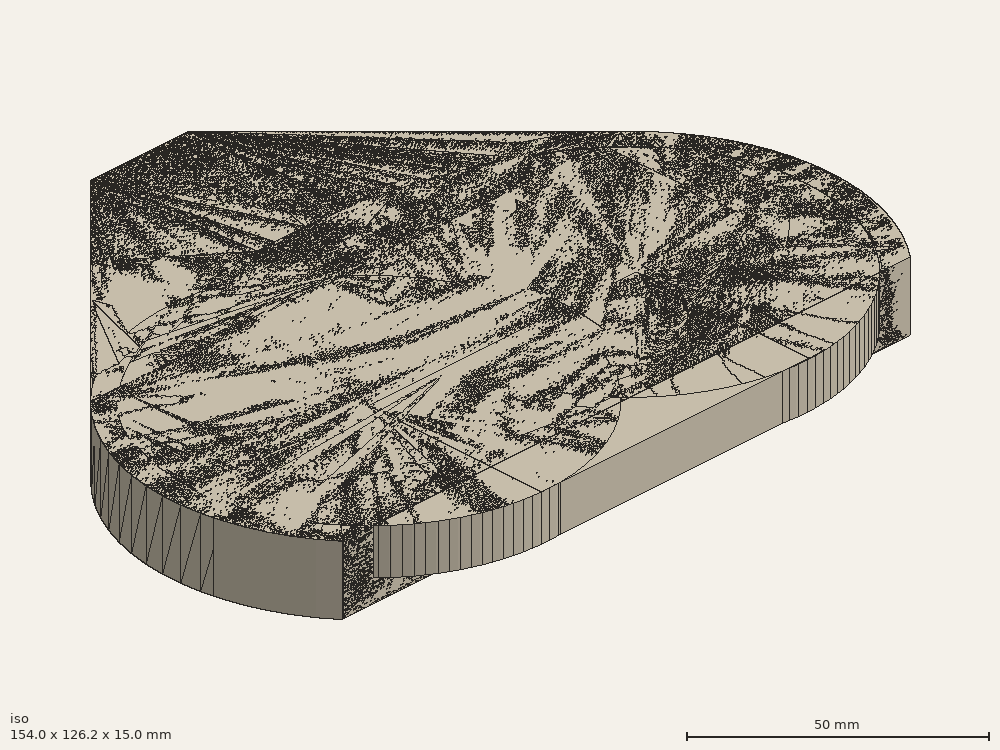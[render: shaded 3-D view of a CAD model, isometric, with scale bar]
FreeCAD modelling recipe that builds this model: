
FCSTD DOCUMENT  (FreeCAD 0.18.4R)
Label: Szajzuhany.Tarto
License: All rights reserved
LicenseURL: http://en.wikipedia.org/wiki/All_rights_reserved
objects: Part::Part2DObjectPython×82, Part::Extrusion×43, Part::Cut×29, Part::Feature×22, Part::MultiFuse×13, Part::FeaturePython×8, Part::Box×6, App::DocumentObjectGroup×4
note: 203 computed .brp shape members not serialized (recipe doc carries the construction recipe); baked Part::Feature solids carry a one-line shape summary decoded from their .brp

FEATURE [Part::Feature] Cut009001_solid  label="Cut010 (Solid)"
  shape: bbox 154 x 114.1 x 15 mm, 51 faces (baked)
FEATURE [Part::Part2DObjectPython] Wire  # Draft 2D object (typed FeaturePython)
  ChamferSize = 0
  Closed = true
  End = (-2.4044,46.1222,15)
  FilletRadius = 0
  Length = 57.6433
  MakeFace = true
  Placement = pos=(-7.75138,65.6617,15) rot=(1,0,0;3.14159rad)
  Points = (4) [(0,0,0),(-8.81629,8.81629,0),(-5.09821,22.4033,-1.11644e-11),(5.34698,19.5396,-1.11644e-11)]
  Start = (-7.75138,65.6617,15)
  Subdivisions = 0
FEATURE [Part::Extrusion] Extrusion
  Base = -> Wire
  Dir = (3.3872e-12,-5.489e-12,-10)
  DirMode = 0
  FaceMakerClass = Part::FaceMakerBullseye
  LengthFwd = 0
  LengthRev = 0
  Solid = true
  Symmetric = false
FEATURE [Part::Part2DObjectPython] Ellipse002  # Draft 2D object (typed FeaturePython)
  FirstAngle = 0
  LastAngle = 0
  MajorRadius = 69
  MakeFace = true
  MinorRadius = 38
  Placement = pos=(22.4696,10.8296,15) rot=(0,0,1;0rad)
FEATURE [Part::Part2DObjectPython] Line  # Draft 2D object (typed FeaturePython)
  ChamferSize = 0
  Closed = false
  End = (22.8586,-51.8037,15)
  FilletRadius = 0
  Length = 136.575
  MakeFace = true
  Placement = pos=(22.8586,84.7717,15) rot=(0,0,1;0rad)
  Points = (2) [(0,0,0),(-3.55271e-15,-136.575,0)]
  Start = (22.8586,84.7717,15)
  Subdivisions = 0
FEATURE [Part::Part2DObjectPython] Circle  # Draft 2D object (typed FeaturePython)
  FirstAngle = 0
  LastAngle = 0
  MakeFace = true
  Placement = pos=(53.0091,0.0899907,15) rot=(0,0,1;0rad)
  Radius = 41.5
  Support = -> [Cut009001_solid]
FEATURE [Part::Part2DObjectPython] Circle001  # Draft 2D object (typed FeaturePython)
  FirstAngle = 0
  LastAngle = 0
  MakeFace = true
  Placement = pos=(-7.41655,0.315657,15) rot=(0,0,1;0rad)
  Radius = 41.5
  Support = -> [Cut009001_solid]
FEATURE [Part::Extrusion] Extrusion001
  Base = -> Circle
  Dir = (0,0,-10)
  DirMode = 0
  FaceMakerClass = Part::FaceMakerBullseye
  LengthFwd = 0
  LengthRev = 0
  Solid = true
  Symmetric = false
FEATURE [Part::Extrusion] Extrusion002
  Base = -> Circle001
  Dir = (0,0,-10)
  DirMode = 0
  FaceMakerClass = Part::FaceMakerBullseye
  LengthFwd = 0
  LengthRev = 0
  Solid = true
  Symmetric = false
FEATURE [Part::MultiFuse] Fusion
  Shapes = -> [Extrusion001,Extrusion002,Extrusion]
FEATURE [Part::Extrusion] Extrusion003
  Base = -> Ellipse002
  Dir = (0,0,-10)
  DirMode = 0
  FaceMakerClass = Part::FaceMakerBullseye
  LengthFwd = 0
  LengthRev = 0
  Solid = true
  Symmetric = false
FEATURE [Part::MultiFuse] Fusion001
  Shapes = -> [Extrusion003,Fusion]
FEATURE [Part::Feature] Fusion001001  label="Fusion002"
  shape: bbox 143.4 x 107.1 x 10 mm, 9 faces (baked)
FEATURE [Part::Part2DObjectPython] Rectangle  # Draft 2D object (typed FeaturePython)
  ChamferSize = 0
  Columns = 1
  FilletRadius = 0
  Height = 40.4113
  Length = 62.7265
  MakeFace = true
  Placement = pos=(-8.86972,-41.0741,15) rot=(0,0,1;0rad)
  Rows = 1
FEATURE [Part::Extrusion] Extrusion004
  Base = -> Rectangle
  Dir = (0,0,-10)
  DirMode = 0
  FaceMakerClass = Part::FaceMakerBullseye
  LengthFwd = 0
  LengthRev = 0
  Solid = true
  Symmetric = false
FEATURE [Part::MultiFuse] Fusion001002
  Shapes = -> [Fusion001001,Extrusion004]
FEATURE [Part::Feature] Fusion001002001  label="Fusion001003"
  shape: bbox 143.4 x 107.1 x 10 mm, 10 faces (baked)
FEATURE [Part::Part2DObjectPython] Line002  # Draft 2D object (typed FeaturePython)
  ChamferSize = 0
  Closed = false
  End = (-40.5133,32.8999,15)
  FilletRadius = 0
  Length = 73.3579
  MakeFace = true
  Placement = pos=(11.3586,84.7717,15) rot=(0,0,1;0rad)
  Points = (2) [(0,0,0),(-51.8718,-51.8718,0)]
  Start = (11.3586,84.7717,15)
  Subdivisions = 0
  Support = -> [Fusion001002]
FEATURE [Part::Part2DObjectPython] Line003  # Draft 2D object (typed FeaturePython)
  ChamferSize = 0
  Closed = false
  End = (86.2304,32.8999,15)
  FilletRadius = 0
  Length = 73.3579
  MakeFace = true
  Placement = pos=(34.3586,84.7717,15) rot=(0,0,1;0rad)
  Points = (2) [(0,0,0),(51.8718,-51.8718,0)]
  Start = (34.3586,84.7717,15)
  Subdivisions = 0
FEATURE [Part::Part2DObjectPython] Line004  # Draft 2D object (typed FeaturePython)
  ChamferSize = 0
  Closed = false
  End = (89.4297,-29.3342,15)
  FilletRadius = 0
  Length = 133.142
  MakeFace = true
  Placement = pos=(-43.7125,-29.3342,15) rot=(0,0,1;0rad)
  Points = (2) [(0,0,0),(133.142,3.69127e-12,-3.93214e-11)]
  Start = (-43.7125,-29.3342,15)
  Subdivisions = 0
FEATURE [Part::Part2DObjectPython] Circle002  # Draft 2D object (typed FeaturePython)
  FirstAngle = 0
  LastAngle = 0
  MakeFace = true
  Placement = pos=(53.5785,0.542169,15) rot=(0,0,1;0rad)
  Radius = 46
FEATURE [Part::Part2DObjectPython] Circle003  # Draft 2D object (typed FeaturePython)
  FirstAngle = 0
  LastAngle = 0
  MakeFace = true
  Placement = pos=(-8.18382,0.175382,15) rot=(0,0,1;0rad)
  Radius = 46
FEATURE [Part::Part2DObjectPython] Line006  # Draft 2D object (typed FeaturePython)
  ChamferSize = 0
  Closed = false
  End = (99.5785,0.542169,15)
  FilletRadius = 0
  Length = 153.763
  MakeFace = true
  Placement = pos=(-54.1838,0.175382,15) rot=(0,0,1;0rad)
  Points = (2) [(0,0,0),(153.762,0.366787,5.44933e-11)]
  Start = (-54.1838,0.175382,15)
  Subdivisions = 0
FEATURE [Part::Part2DObjectPython] Line007  # Draft 2D object (typed FeaturePython)
  ChamferSize = 0
  Closed = false
  End = (-8.18382,0.175382,15)
  FilletRadius = 0
  Length = 46
  MakeFace = true
  Placement = pos=(-54.1838,0.175382,15) rot=(0,0,1;0rad)
  Points = (2) [(0,0,0),(46,1.33227e-15,-3.55271e-15)]
  Start = (-54.1838,0.175382,15)
  Subdivisions = 0
FEATURE [Part::Part2DObjectPython] Line008  # Draft 2D object (typed FeaturePython)
  ChamferSize = 0
  Closed = false
  End = (53.5785,0.542169,15)
  FilletRadius = 0
  Length = 46
  MakeFace = true
  Placement = pos=(99.5785,0.542169,15) rot=(0,0,1;0rad)
  Points = (2) [(0,0,0),(-46,-1.44329e-15,0)]
  Start = (99.5785,0.542169,15)
  Subdivisions = 0
FEATURE [Part::Part2DObjectPython] Rectangle001  # Draft 2D object (typed FeaturePython)
  ChamferSize = 0
  Columns = 1
  FilletRadius = 0
  Height = 26.0422
  Length = 146.972
  MakeFace = true
  Placement = pos=(-43.7125,-55.3763,15) rot=(0,0,1;0rad)
  Rows = 1
FEATURE [Part::Extrusion] Extrusion005
  Base = -> Circle002
  Dir = (-1.237e-13,-1.344e-13,-15)
  DirMode = 0
  FaceMakerClass = Part::FaceMakerBullseye
  LengthFwd = 0
  LengthRev = 0
  Solid = true
  Symmetric = false
FEATURE [Part::Extrusion] Extrusion006
  Base = -> Circle003
  Dir = (-1.2e-13,-1.35e-13,-15)
  DirMode = 0
  FaceMakerClass = Part::FaceMakerBullseye
  LengthFwd = 0
  LengthRev = 0
  Solid = true
  Symmetric = false
FEATURE [Part::Extrusion] Extrusion007
  Base = -> Rectangle001
  Dir = (-9.0068e-12,-2.3018e-12,-15)
  DirMode = 0
  FaceMakerClass = Part::FaceMakerBullseye
  LengthFwd = 0
  LengthRev = 0
  Solid = true
  Symmetric = false
FEATURE [Part::MultiFuse] Fusion001002002
  Shapes = -> [Extrusion006,Extrusion005]
FEATURE [Part::Cut] Cut
  Base = -> Fusion001002002
  Tool = -> Extrusion007
FEATURE [Part::Part2DObjectPython] Wire001  # Draft 2D object (typed FeaturePython)
  ChamferSize = 0
  Closed = true
  End = (86.2304,32.8999,15)
  FilletRadius = 0
  Length = 296.459
  MakeFace = true
  Placement = pos=(-40.5133,32.8999,15) rot=(0,0,1;0rad)
  Points = (4) [(0,0,0),(51.8718,51.8718,3.91047e-11),(74.8718,51.8718,1.35945e-11),(126.744,5.65221e-07,3.67812e-11)]
  Start = (-40.5133,32.8999,15)
  Subdivisions = 0
FEATURE [Part::Extrusion] Extrusion008
  Base = -> Wire001
  Dir = (-4.9814e-12,-2e-16,-15)
  DirMode = 0
  FaceMakerClass = Part::FaceMakerBullseye
  LengthFwd = 0
  LengthRev = 0
  Solid = true
  Symmetric = false
FEATURE [Part::MultiFuse] Fusion001002003
  Shapes = -> [Cut,Extrusion008]
FEATURE [Part::Feature] Fusion001002003001  label="Fusion001002004"
  shape: bbox 153.8 x 114.1 x 15 mm, 9 faces (baked)
FEATURE [Part::Cut] Cut001
  Base = -> Fusion001002003001
  Tool = -> Fusion001002001
FEATURE [Part::Part2DObjectPython] Line009  # Draft 2D object (typed FeaturePython)
  ChamferSize = 0
  Closed = false
  End = (-4.28911,53.0095,15)
  FilletRadius = 0
  Length = 10.8307
  MakeFace = true
  Placement = pos=(-14.7357,50.1508,15) rot=(0,0,1;0rad)
  Points = (2) [(0,0,0),(10.4466,2.85869,4.25615e-12)]
  Start = (-14.7357,50.1508,15)
  Subdivisions = 0
  Support = -> [Cut001]
FEATURE [Part::Part2DObjectPython] Line010  # Draft 2D object (typed FeaturePython)
  ChamferSize = 0
  Closed = false
  End = (-6.85861,41.8824,15)
  FilletRadius = 0
  Length = 20.1087
  MakeFace = true
  Placement = pos=(-12.1662,61.2779,15) rot=(0,0,1;0rad)
  Points = (2) [(0,0,0),(5.30757,-19.3956,9.64029e-12)]
  Start = (-12.1662,61.2779,15)
  Subdivisions = 0
FEATURE [Part::Part2DObjectPython] Line011  # Draft 2D object (typed FeaturePython)
  ChamferSize = 0
  Closed = false
  End = (1.96496,47.525,15)
  FilletRadius = 0
  Length = 20
  MakeFace = true
  Placement = pos=(-17.3258,42.2461,15) rot=(0,0,1;0rad)
  Points = (2) [(0,0,0),(19.2908,5.27889,6.31317e-12)]
  Start = (-17.3258,42.2461,15)
  Subdivisions = 0
FEATURE [Part::Part2DObjectPython] Wire002  # Draft 2D object (typed FeaturePython)
  ChamferSize = 0
  Closed = true
  End = (1.96496,47.525,15)
  FilletRadius = 0
  Length = 47.4672
  MakeFace = true
  Placement = pos=(-17.3258,42.2461,15) rot=(0,0,1;0rad)
  Points = (4) [(0,0,0),(2.59011,7.90474,-2.29683e-12),(13.0367,10.7634,1.95932e-12),(19.2908,5.27889,6.31317e-12)]
  Start = (-17.3258,42.2461,15)
  Subdivisions = 0
FEATURE [Part::Part2DObjectPython] Line012  # Draft 2D object (typed FeaturePython)
  ChamferSize = 0
  Closed = false
  End = (-2.44381,46.2662,5)
  FilletRadius = 0
  Length = 10.8308
  MakeFace = true
  Placement = pos=(-12.9037,43.4562,5) rot=(0,0,1;0rad)
  Points = (2) [(0,0,0),(10.4599,2.81,1.53388e-11)]
  Start = (-12.9037,43.4562,5)
  Subdivisions = 0
FEATURE [Part::Extrusion] Extrusion009
  Base = -> Wire002
  Dir = (8.734e-13,-2.6174e-12,-10)
  DirMode = 0
  FaceMakerClass = Part::FaceMakerBullseye
  LengthFwd = 0
  LengthRev = 0
  Solid = true
  Symmetric = false
FEATURE [Part::Feature] Face
  shape: bbox 19.29 x 5.279 x 10 mm, 1 faces, 0 solids (baked)
FEATURE [Part::Extrusion] Extrusion010
  Base = -> Face
  Dir = (0.821807,-3.00314,8.578e-13)
  DirMode = 0
  FaceMakerClass = Part::FaceMakerBullseye
  LengthFwd = 0
  LengthRev = 0
  Solid = true
  Symmetric = false
FEATURE [Part::MultiFuse] Fusion001002003002
  Shapes = -> [Extrusion009,Extrusion010]
FEATURE [Part::Feature] Fusion001002003002001  label="Fusion001002003003"
  shape: bbox 20.11 x 13.77 x 10 mm, 8 faces (baked)
FEATURE [Part::Cut] Cut002
  Base = -> Cut001
  Tool = -> Fusion001002003002001
FEATURE [Part::Part2DObjectPython] Line014  # Draft 2D object (typed FeaturePython)
  ChamferSize = 0
  Closed = false
  End = (84.8846,34.2456,15)
  FilletRadius = 0
  Length = 34.7757
  MakeFace = true
  Placement = pos=(60.2945,58.8358,15) rot=(0,0,1;0rad)
  Points = (2) [(0,0,0),(24.5901,-24.5901,1.92788e-11)]
  Start = (60.2945,58.8358,15)
  Subdivisions = 0
  Support = -> [Cut002]
FEATURE [Part::Part2DObjectPython] Line015  # Draft 2D object (typed FeaturePython)
  ChamferSize = 0
  Closed = false
  End = (72.5896,46.5407,5)
  FilletRadius = 0
  Length = 10
  MakeFace = true
  Placement = pos=(72.5896,46.5407,15) rot=(0.281085,0.678598,0.678598;2.59356rad)
  Points = (2) [(0,0,0),(3.07523e-11,-10,-1.27471e-11)]
  Start = (72.5896,46.5407,15)
  Subdivisions = 0
FEATURE [Part::Part2DObjectPython] Circle004  # Draft 2D object (typed FeaturePython)
  FirstAngle = 0
  LastAngle = 0
  MakeFace = true
  Placement = pos=(72.5896,46.5407,10) rot=(0.281085,0.678598,0.678598;2.59356rad)
  Radius = 2.1
FEATURE [Part::Part2DObjectPython] Rectangle002  # Draft 2D object (typed FeaturePython)
  ChamferSize = 0
  Columns = 1
  FilletRadius = 0
  Height = 26.5449
  Length = 18.0281
  MakeFace = true
  Placement = pos=(41.0717,40.5184,10) rot=(0,0,-1;0.785398rad)
  Rows = 1
FEATURE [Part::Extrusion] Extrusion011
  Base = -> Circle004
  Dir = (-18.7701,-18.7701,-2.75929e-11)
  DirMode = 0
  FaceMakerClass = Part::FaceMakerBullseye
  LengthFwd = 0
  LengthRev = 0
  Solid = true
  Symmetric = false
FEATURE [Part::Cut] Cut003
  Base = -> Cut002
  Tool = -> Extrusion011
FEATURE [Part::Part2DObjectPython] Line016  # Draft 2D object (typed FeaturePython)
  ChamferSize = 0
  Closed = false
  End = (-14.5773,58.8358,15)
  FilletRadius = 0
  Length = 36.6789
  MakeFace = true
  Placement = pos=(-40.5133,32.8999,15) rot=(-0.862856,-0.357407,0.357407;1.71777rad)
  Points = (2) [(0,0,0),(36.6789,8.60823e-12,-7.10543e-15)]
  Start = (-40.5133,32.8999,15)
  Subdivisions = 0
  Support = -> [Cut003]
FEATURE [Part::Part2DObjectPython] Line017  # Draft 2D object (typed FeaturePython)
  ChamferSize = 0
  Closed = false
  End = (-27.5453,45.8678,5)
  FilletRadius = 0
  Length = 10
  MakeFace = true
  Placement = pos=(-27.5453,45.8678,15) rot=(-0.862856,-0.357407,0.357407;1.71777rad)
  Points = (2) [(0,0,0),(-2.34657e-12,10,-2.84217e-14)]
  Start = (-27.5453,45.8678,15)
  Subdivisions = 0
FEATURE [Part::Part2DObjectPython] Line018  # Draft 2D object (typed FeaturePython)
  ChamferSize = 0
  Closed = false
  End = (-27.5453,45.8678,15)
  FilletRadius = 0
  Length = 18.3395
  MakeFace = true
  Placement = pos=(-40.5133,32.8999,15) rot=(-0.862856,-0.357407,0.357407;1.71777rad)
  Points = (2) [(0,0,0),(18.3395,4.30589e-12,7.10543e-15)]
  Start = (-40.5133,32.8999,15)
  Subdivisions = 0
FEATURE [Part::Part2DObjectPython] Circle005  # Draft 2D object (typed FeaturePython)
  FirstAngle = 0
  LastAngle = 0
  MakeFace = true
  Placement = pos=(-27.5453,45.8678,10) rot=(-0.862856,-0.357407,0.357407;1.71777rad)
  Radius = 2.1
FEATURE [Part::Part2DObjectPython] Rectangle003  # Draft 2D object (typed FeaturePython)
  ChamferSize = 0
  Columns = 1
  FilletRadius = 0
  Height = 11.696
  Length = 15.5444
  MakeFace = true
  Placement = pos=(-30.2665,26.606,10) rot=(0,0,1;0.785398rad)
  Rows = 1
  Support = -> [Cut003]
FEATURE [Part::Extrusion] Extrusion012
  Base = -> Circle005
  Dir = (8.27029,-8.27029,-2.7481e-12)
  DirMode = 0
  FaceMakerClass = Part::FaceMakerBullseye
  LengthFwd = 0
  LengthRev = 0
  Solid = true
  Symmetric = false
FEATURE [Part::Cut] Cut004
  Base = -> Cut003
  Tool = -> Extrusion012
FEATURE [Part::Part2DObjectPython] Circle006  # Draft 2D object (typed FeaturePython)
  FirstAngle = 0
  LastAngle = 0
  MakeFace = true
  Placement = pos=(-19.414,37.4585,10) rot=(-0.862856,-0.357407,0.357407;1.71777rad)
  Radius = 3.5
  Support = -> [Cut004]
FEATURE [Part::Part2DObjectPython] Circle007  # Draft 2D object (typed FeaturePython)
  FirstAngle = 0
  LastAngle = 0
  MakeFace = true
  Placement = pos=(53.8195,27.7706,10) rot=(-0.862856,0.357407,-0.357407;1.71777rad)
  Radius = 3.5
  Support = -> [Cut004]
FEATURE [Part::Part2DObjectPython] Line019  # Draft 2D object (typed FeaturePython)
  ChamferSize = 0
  Closed = false
  End = (62.6801,49.3791,10)
  FilletRadius = 0
  Length = 5
  MakeFace = true
  Placement = pos=(66.2157,52.9146,10) rot=(0,0,-1;0.785398rad)
  Points = (2) [(0,0,0),(0,-5,-3.55271e-15)]
  Start = (66.2157,52.9146,10)
  Subdivisions = 0
  Support = -> [Rectangle002]
FEATURE [Part::Extrusion] Extrusion013
  Base = -> Circle007
  Dir = (15.2345,15.2345,-5.0648e-12)
  DirMode = 0
  FaceMakerClass = Part::FaceMakerBullseye
  LengthFwd = 0
  LengthRev = 0
  Solid = true
  Symmetric = false
FEATURE [Part::Part2DObjectPython] Line020  # Draft 2D object (typed FeaturePython)
  ChamferSize = 0
  Closed = false
  End = (-29.5055,36.8365,10)
  FilletRadius = 0
  Length = 5
  MakeFace = true
  Placement = pos=(-33.0411,40.3721,10) rot=(0,0,-1;0.785398rad)
  Points = (2) [(0,0,0),(5,1.63446e-07,0)]
  Start = (-33.0411,40.3721,10)
  Subdivisions = 0
FEATURE [Part::Extrusion] Extrusion014
  Base = -> Circle006
  Dir = (-6.50253,6.50253,2.1607e-12)
  DirMode = 0
  FaceMakerClass = Part::FaceMakerBullseye
  LengthFwd = 0
  LengthRev = 0
  Solid = true
  Symmetric = false
FEATURE [Part::Cut] Cut005
  Base = -> Cut004
  Tool = -> Extrusion013
FEATURE [Part::Cut] Cut006
  Base = -> Cut005
  Tool = -> Extrusion014
FEATURE [Part::Part2DObjectPython] Line021  # Draft 2D object (typed FeaturePython)
  ChamferSize = 0
  Closed = false
  End = (22.8586,79.7717,15)
  FilletRadius = 0
  Length = 5
  MakeFace = true
  Placement = pos=(22.8586,84.7717,15) rot=(0,0,1;0rad)
  Points = (2) [(0,0,0),(-1.36695e-16,-5,0)]
  Start = (22.8586,84.7717,15)
  Subdivisions = 0
FEATURE [Part::Part2DObjectPython] Line022  # Draft 2D object (typed FeaturePython)
  ChamferSize = 0
  Closed = false
  End = (47.1156,79.7717,15)
  FilletRadius = 0
  Length = 48.5141
  MakeFace = true
  Placement = pos=(-1.39846,79.7717,15) rot=(0,0,1;0rad)
  Points = (2) [(0,0,0),(48.5141,0,0)]
  Start = (-1.39846,79.7717,15)
  Subdivisions = 0
FEATURE [Part::Part2DObjectPython] Line023  # Draft 2D object (typed FeaturePython)
  ChamferSize = 0
  Closed = false
  End = (-4.21585,62.1262,15)
  FilletRadius = 0
  Length = 27.0256
  MakeFace = true
  Placement = pos=(14.8941,81.2362,15) rot=(0,0,1;0rad)
  Points = (2) [(0,0,0),(-19.11,-19.11,-1.83675e-12)]
  Start = (14.8941,81.2362,15)
  Subdivisions = 0
FEATURE [Part::Part2DObjectPython] Line024  # Draft 2D object (typed FeaturePython)
  ChamferSize = 0
  Closed = false
  End = (1.8036,75.2167,15)
  FilletRadius = 0
  Length = 5
  MakeFace = true
  Placement = pos=(5.33913,71.6812,15) rot=(0,0,1;0rad)
  Points = (2) [(0,0,0),(-3.53553,3.53553,-3.55271e-15)]
  Start = (5.33913,71.6812,15)
  Subdivisions = 0
FEATURE [Part::Part2DObjectPython] Line025  # Draft 2D object (typed FeaturePython)
  ChamferSize = 0
  Closed = false
  End = (81.3491,30.7101,15)
  FilletRadius = 0
  Length = 71.4547
  MakeFace = true
  Placement = pos=(30.823,81.2362,15) rot=(0,0,1;0rad)
  Points = (2) [(0,0,0),(50.5261,-50.5261,3.14593e-11)]
  Start = (30.823,81.2362,15)
  Subdivisions = 0
FEATURE [Part::Part2DObjectPython] Line026  # Draft 2D object (typed FeaturePython)
  ChamferSize = 0
  Closed = false
  End = (59.6216,59.5087,15)
  FilletRadius = 0
  Length = 5
  MakeFace = true
  Placement = pos=(56.0861,55.9731,15) rot=(0,0,1;0rad)
  Points = (2) [(0,0,0),(3.53553,3.53553,3.55271e-15)]
  Start = (56.0861,55.9731,15)
  Subdivisions = 0
FEATURE [Part::Part2DObjectPython] Line027  # Draft 2D object (typed FeaturePython)
  ChamferSize = 0
  Closed = false
  End = (0.533579,54.3292,15)
  FilletRadius = 0
  Length = 13.1174
  MakeFace = true
  Placement = pos=(-2.92869,66.9815,15) rot=(0,0,1;0rad)
  Points = (2) [(0,0,0),(3.46227,-12.6522,6.28475e-12)]
  Start = (-2.92869,66.9815,15)
  Subdivisions = 0
FEATURE [Part::Part2DObjectPython] Line028  # Draft 2D object (typed FeaturePython)
  ChamferSize = 0
  Closed = false
  End = (-6.02025,59.3356,15)
  FilletRadius = 0
  Length = 5
  MakeFace = true
  Placement = pos=(-1.19756,60.6553,15) rot=(0,0,1;0rad)
  Points = (2) [(0,0,0),(-4.82269,-1.31972,0)]
  Start = (-1.19756,60.6553,15)
  Subdivisions = 0
FEATURE [Part::Part2DObjectPython] Line029  # Draft 2D object (typed FeaturePython)
  ChamferSize = 0
  Closed = false
  End = (5.50049,51.0605,15)
  FilletRadius = 0
  Length = 8.31827
  MakeFace = true
  Placement = pos=(-0.753577,56.545,15) rot=(0,0,1;0rad)
  Points = (2) [(0,0,0),(6.25407,-5.48455,4.35918e-12)]
  Start = (-0.753577,56.545,15)
  Subdivisions = 0
  Support = -> [Cut006]
FEATURE [Part::Part2DObjectPython] Line030  # Draft 2D object (typed FeaturePython)
  ChamferSize = 0
  Closed = false
  End = (-1.16208,50.2672,15)
  FilletRadius = 0
  Length = 5
  MakeFace = true
  Placement = pos=(2.37346,53.8028,15) rot=(0,0,1;0rad)
  Points = (2) [(0,0,0),(-3.53553,-3.53553,-8.88178e-15)]
  Start = (2.37346,53.8028,15)
  Subdivisions = 0
  Support = -> [Cut006]
FEATURE [Part::Part2DObjectPython] Wire003  # Draft 2D object (typed FeaturePython)
  ChamferSize = 0
  Closed = true
  End = (6.2674,51.6562,15)
  FilletRadius = 0
  Length = 173.393
  MakeFace = true
  Placement = pos=(5.50049,51.0605,15) rot=(0,0,1;0rad)
  Points = (14) [(0,0,0),(-5.36621,4.71603,-1.79305e-11),(-7.61093,13.1476,-1.79305e-11),(7.93343,28.7313,-1.79305e-11),(26.7671,28.7401,-1.79305e-11),+9 more]
  Start = (5.50049,51.0605,15)
  Subdivisions = 0
FEATURE [Part::Feature] Face001
  shape: bbox 143.4 x 78.16 x 3e-07 mm, 1 faces, 0 solids (baked)
FEATURE [Part::Extrusion] Extrusion015
  Base = -> Face001
  Dir = (-1.173e-13,1.24e-14,-1)
  DirMode = 0
  FaceMakerClass = Part::FaceMakerBullseye
  LengthFwd = 0
  LengthRev = 0
  Solid = true
  Symmetric = false
FEATURE [Part::Cut] Cut007
  Base = -> Cut006
  Tool = -> Extrusion015
FEATURE [Part::Feature] Face002
  shape: bbox 19.29 x 5.279 x 1 mm, 1 faces, 0 solids (baked)
FEATURE [Part::Extrusion] Extrusion016
  Base = -> Face002
  Dir = (-0.7141,2.60955,1.162e-13)
  DirMode = 0
  FaceMakerClass = Part::FaceMakerBullseye
  LengthFwd = 0
  LengthRev = 0
  Solid = true
  Symmetric = false
FEATURE [Part::Cut] Cut008
  Base = -> Cut007
  Tool = -> Extrusion016
FEATURE [Part::Extrusion] Extrusion017
  Base = -> Wire003
  Dir = (-4.3113e-12,7.009e-13,-11)
  DirMode = 0
  FaceMakerClass = Part::FaceMakerBullseye
  LengthFwd = 0
  LengthRev = 0
  Placement = pos=(-1.577e-12,2.42e-13,-4) rot=(0,0,1;0rad)
  Solid = true
  Symmetric = false
FEATURE [Part::Part2DObjectPython] Line033  # Draft 2D object (typed FeaturePython)
  ChamferSize = 0
  Closed = false
  End = (32.2676,79.8006,-2.99924e-11)
  FilletRadius = 0
  Length = 5.39296
  MakeFace = true
  Placement = pos=(34.3586,84.7717,-3.0521e-11) rot=(1,0,0;3.14159rad)
  Points = (2) [(0,0,0),(-2.09094,4.97112,-1.01357e-12)]
  Start = (34.3586,84.7717,-3.0521e-11)
  Subdivisions = 0
FEATURE [Part::Part2DObjectPython] Rectangle004  # Draft 2D object (typed FeaturePython)
  ChamferSize = 0
  Columns = 1
  FilletRadius = 0
  Height = 31.6287
  Length = 27.0047
  MakeFace = true
  Placement = pos=(62.9263,63.4763,-1.6004e-11) rot=(1,0,0;3.14159rad)
  Rows = 1
  Support = -> [Cut008]
FEATURE [Part::Extrusion] Extrusion018
  Base = -> Rectangle004
  Dir = (2.3659e-12,-2.0725e-12,11)
  DirMode = 0
  FaceMakerClass = Part::FaceMakerBullseye
  LengthFwd = 0
  LengthRev = 0
  Solid = true
  Symmetric = false
FEATURE [Part::Cut] Cut009
  Base = -> Extrusion017
  Tool = -> Extrusion018
FEATURE [Part::Cut] Cut010
  Base = -> Cut008
  Tool = -> Cut009
FEATURE [Part::Part2DObjectPython] Rectangle005  # Draft 2D object (typed FeaturePython)
  ChamferSize = 0
  Columns = 1
  FilletRadius = 0
  Height = 65
  Length = 50
  MakeFace = true
  Placement = pos=(-2.10694,-23.0493,4) rot=(0,0,1;0rad)
  Rows = 1
FEATURE [Part::Feature] Cut010001  label="Cut011"
  shape: bbox 153.8 x 114.1 x 15 mm, 48 faces (baked)
FEATURE [Part::Feature] Face003
  shape: bbox 19.4 x 23.81 x 3e-07 mm, 1 faces, 0 solids (baked)
FEATURE [Part::Extrusion] Extrusion019
  Base = -> Face003
  Dir = (2.885e-13,-7.237e-13,-1)
  DirMode = 0
  FaceMakerClass = Part::FaceMakerBullseye
  LengthFwd = 0
  LengthRev = 0
  Solid = true
  Symmetric = false
FEATURE [Part::Cut] Cut010002
  Base = -> Cut010001
  Tool = -> Extrusion019
FEATURE [Part::Feature] Cut010002001  label="Cut010003"
  shape: bbox 153.8 x 114.1 x 15 mm, 45 faces (baked)
FEATURE [Part::Feature] Cut010002001001  label="Cut010004"
  shape: bbox 153.8 x 114.1 x 15 mm, 45 faces (baked)
FEATURE [Part::Part2DObjectPython] Line034  # Draft 2D object (typed FeaturePython)
  ChamferSize = 0
  Closed = true
  End = (2.07267,47.1314,15)
  FilletRadius = 0
  Length = 0
  MakeFace = true
  Placement = pos=(2.07267,47.1314,15) rot=(0,0,1;0rad)
  Points = (2) [(0,0,0),(0,0,0)]
  Start = (2.07267,47.1314,15)
  Subdivisions = 0
FEATURE [Part::Part2DObjectPython] Wire004  # Draft 2D object (typed FeaturePython)
  ChamferSize = 0
  Closed = true
  End = (47.8931,30.4354,4)
  FilletRadius = 0
  Length = 124.129
  MakeFace = true
  Placement = pos=(47.9186,45.8969,4) rot=(0,0,1;0rad)
  Points = (7) [(0,0,0),(-8.17559,1.71653,4.44089e-16),(-23.0265,2.92898,4.44089e-16),(-34.5027,2.63361,0),(-45.8401,1.2331,4.44089e-16),+2 more]
  Start = (47.9186,45.8969,4)
  Subdivisions = 0
FEATURE [Part::Extrusion] Extrusion020
  Base = -> Rectangle005
  Dir = (-4.691e-13,4.97e-14,-4)
  DirMode = 0
  FaceMakerClass = Part::FaceMakerBullseye
  LengthFwd = 0
  LengthRev = 0
  Solid = true
  Symmetric = false
FEATURE [Part::Cut] Cut010002001002
  Base = -> Cut010002001001
  Tool = -> Extrusion020
FEATURE [Part::Extrusion] Extrusion021
  Base = -> Wire004
  Dir = (-4.863e-13,1.504e-13,-4)
  DirMode = 0
  FaceMakerClass = Part::FaceMakerBullseye
  LengthFwd = 0
  LengthRev = 0
  Solid = true
  Symmetric = false
FEATURE [Part::Cut] Cut010002001003
  Base = -> Cut010002001002
  Tool = -> Extrusion021
FEATURE [Part::Part2DObjectPython] Wire005  # Draft 2D object (typed FeaturePython)
  ChamferSize = 0
  Closed = true
  End = (2.07847,41.9507,4)
  FilletRadius = 0
  Length = 16.0238
  MakeFace = true
  Placement = pos=(2.07847,47.13,4) rot=(0,0,1;0rad)
  Points = (3) [(0,0,0),(-4.18541,-5.17935,-4.94271e-13),(0,-5.17935,-2.58016e-13)]
  Start = (2.07847,47.13,4)
  Subdivisions = 0
FEATURE [Part::Extrusion] Extrusion022
  Base = -> Wire005
  Dir = (-2.247e-13,2.78e-13,-4)
  DirMode = 0
  FaceMakerClass = Part::FaceMakerBullseye
  LengthFwd = 0
  LengthRev = 0
  Solid = true
  Symmetric = false
FEATURE [Part::Cut] Cut010002001004
  Base = -> Cut010002001003
  Tool = -> Extrusion022
FEATURE [Part::Part2DObjectPython] Wire006  # Draft 2D object (typed FeaturePython)
  ChamferSize = 0
  Closed = true
  End = (6.2674,51.6562,-2.3941e-11)
  FilletRadius = 0
  Length = 15.2695
  MakeFace = true
  Placement = pos=(11.2047,53.1196,-2.553e-11) rot=(0,0,1;0rad)
  Points = (4) [(0,0,0),(-7.16376,-0.776446,1.47227e-11),(-5.70425,-2.05912,1.91241e-11),(-4.93734,-1.46338,1.06038e-12)]
  Start = (11.2047,53.1196,-2.55298e-11)
  Subdivisions = 0
  Support = -> [Cut010002001004]
FEATURE [Part::Extrusion] Extrusion023
  Base = -> Wire006
  Dir = (2.48553e-11,-1.25004e-11,11)
  DirMode = 0
  FaceMakerClass = Part::FaceMakerBullseye
  LengthFwd = 0
  LengthRev = 0
  Solid = true
  Symmetric = false
FEATURE [Part::MultiFuse] Fusion001002003002002
  Shapes = -> [Cut010002001004,Extrusion023]
FEATURE [Part::Feature] Fusion001002003002002001  label="Fusion001002003002003"
  shape: bbox 153.8 x 114.1 x 15 mm, 56 faces (baked)
FEATURE [Part::Part2DObjectPython] Ellipse  # Draft 2D object (typed FeaturePython)
  FirstAngle = 0
  LastAngle = 0
  MajorRadius = 34.47
  MakeFace = true
  MinorRadius = 17
  Placement = pos=(47.9058,11.4238,4) rot=(0,0,1;1.5708rad)
  Support = -> [Fusion001002003002002001]
FEATURE [Part::Part2DObjectPython] Ellipse003  # Draft 2D object (typed FeaturePython)
  FirstAngle = 0
  LastAngle = 0
  MajorRadius = 34.47
  MakeFace = true
  MinorRadius = 17
  Placement = pos=(-2.10694,11.4207,4) rot=(0,0,1;1.5708rad)
  Support = -> [Fusion001002003002002001]
FEATURE [Part::Part2DObjectPython] Wire007  # Draft 2D object (typed FeaturePython)
  ChamferSize = 0
  Closed = true
  End = (-0.621533,43.7888,4)
  FilletRadius = 0
  Length = 11.0612
  MakeFace = true
  Placement = pos=(2.07847,47.13,4) rot=(0,0,1;0rad)
  Points = (3) [(0,0,0),(-4.18541,-3.20935,-2.4869e-13),(-2.7,-3.34119,-2.4869e-13)]
  Start = (2.07847,47.13,4)
  Subdivisions = 0
  Support = -> [Ellipse003]
FEATURE [Part::Part2DObjectPython] Wire008  # Draft 2D object (typed FeaturePython)
  ChamferSize = 0
  Closed = true
  End = (0.695781,45.419,4)
  FilletRadius = 0
  Length = 13.2439
  MakeFace = true
  Placement = pos=(2.07847,47.13,4) rot=(0,0,1;0rad)
  Points = (3) [(0,0,0),(-6.12381,-1.4642,1.5671e-11),(-1.38268,-1.71104,-1.62981e-13)]
  Start = (2.07847,47.13,4)
  Subdivisions = 0
FEATURE [Part::Extrusion] Extrusion024
  Base = -> Wire008
  Dir = (-1.32517e-11,1.08054e-11,-4)
  DirMode = 0
  FaceMakerClass = Part::FaceMakerBullseye
  LengthFwd = 0
  LengthRev = 0
  Solid = true
  Symmetric = false
FEATURE [Part::Cut] Cut010002001005
  Base = -> Fusion001002003002002001
  Tool = -> Extrusion024
FEATURE [Part::Extrusion] Extrusion025
  Base = -> Ellipse003
  Dir = (-4.52e-13,8e-14,-4)
  DirMode = 0
  FaceMakerClass = Part::FaceMakerBullseye
  LengthFwd = 0
  LengthRev = 0
  Solid = true
  Symmetric = false
FEATURE [Part::Cut] Cut010002001006
  Base = -> Cut010002001005
  Tool = -> Extrusion025
FEATURE [Part::Extrusion] Extrusion026
  Base = -> Ellipse
  Dir = (-4.509e-13,7.91e-14,-4)
  DirMode = 0
  FaceMakerClass = Part::FaceMakerBullseye
  LengthFwd = 0
  LengthRev = 0
  Solid = true
  Symmetric = false
FEATURE [Part::Cut] Cut010002001007
  Base = -> Cut010002001006
  Tool = -> Extrusion026
FEATURE [Part::Part2DObjectPython] Wire011  # Draft 2D object (typed FeaturePython)
  ChamferSize = 0
  Closed = true
  End = (44.4673,39.2999,4)
  FilletRadius = 0
  Length = 21.2667
  MakeFace = true
  Placement = pos=(39.743,47.6134,4) rot=(0,0,1;0rad)
  Points = (3) [(0,0,0),(3.92481,-0.624572,2.10232e-11),(4.72427,-8.31353,-8.88178e-16)]
  Start = (39.743,47.6134,4)
  Subdivisions = 0
FEATURE [Part::Part2DObjectPython] Wire012  # Draft 2D object (typed FeaturePython)
  ChamferSize = 0
  Closed = true
  End = (44.4673,39.2999,4)
  FilletRadius = 0
  Length = 17.9354
  MakeFace = true
  Placement = pos=(43.6678,46.9889,4) rot=(0,0,1;0rad)
  Points = (3) [(0,0,0),(2.73271,-0.522339,3.18856e-13),(0.799458,-7.68896,-2.10245e-11)]
  Start = (43.6678,46.9889,4)
  Subdivisions = 0
FEATURE [Part::Part2DObjectPython] Wire013  # Draft 2D object (typed FeaturePython)
  ChamferSize = 0
  Closed = true
  End = (44.4673,39.2999,4)
  FilletRadius = 0
  Length = 17.0627
  MakeFace = true
  Placement = pos=(46.4005,46.4665,4) rot=(0,0,1;0rad)
  Points = (3) [(0,0,0),(1.84056,-0.387058,0.000492573),(-1.93325,-7.16662,-2.13429e-11)]
  Start = (46.4005,46.4665,4)
  Subdivisions = 0
FEATURE [Part::Part2DObjectPython] Wire014  # Draft 2D object (typed FeaturePython)
  ChamferSize = 0
  Closed = true
  End = (49.022,40.9401,4)
  FilletRadius = 0
  Length = 11.3598
  MakeFace = true
  Placement = pos=(48.2411,46.0795,4.00049) rot=(0,0,1;0rad)
  Points = (3) [(0,0,0),(1.29469,-0.345387,-0.000492573),(0.780976,-5.13939,-0.000492573)]
  Start = (48.2411,46.0795,4.00049)
  Subdivisions = 0
FEATURE [Part::Part2DObjectPython] Wire015  # Draft 2D object (typed FeaturePython)
  ChamferSize = 0
  Closed = true
  End = (49.022,40.9401,4)
  FilletRadius = 0
  Length = 17.7986
  MakeFace = true
  Placement = pos=(44.4673,39.2999,4) rot=(0,0,1;0rad)
  Points = (3) [(0,0,0),(3.77381,6.77956,0.000492573),(4.55478,1.64017,-2.66454e-15)]
  Start = (44.4673,39.2999,4)
  Subdivisions = 0
FEATURE [Part::Extrusion] Extrusion027
  Base = -> Wire014
  Dir = (-0.00147975,0.000158567,-4.0006)
  DirMode = 0
  FaceMakerClass = Part::FaceMakerBullseye
  LengthFwd = 0
  LengthRev = 0
  Solid = true
  Symmetric = false
FEATURE [Part::Cut] Cut010002001008
  Base = -> Cut010002001007
  Tool = -> Extrusion027
FEATURE [Part::Extrusion] Extrusion028
  Base = -> Wire015
  Dir = (-0.000130905,0.000363525,-4.00049)
  DirMode = 0
  FaceMakerClass = Part::FaceMakerBullseye
  LengthFwd = 0
  LengthRev = 0
  Solid = true
  Symmetric = false
FEATURE [Part::Extrusion] Extrusion029
  Base = -> Wire013
  Dir = (0.00101323,-0.000273327,-4.00084)
  DirMode = 0
  FaceMakerClass = Part::FaceMakerBullseye
  LengthFwd = 0
  LengthRev = 0
  Solid = true
  Symmetric = false
FEATURE [Part::Extrusion] Extrusion030
  Base = -> Wire012
  Dir = (2.1582e-12,1.12876e-11,-4)
  DirMode = 0
  FaceMakerClass = Part::FaceMakerBullseye
  LengthFwd = 0
  LengthRev = 0
  Solid = true
  Symmetric = false
FEATURE [Part::Extrusion] Extrusion031
  Base = -> Wire011
  Dir = (2.31052e-11,1.34656e-11,-4)
  DirMode = 0
  FaceMakerClass = Part::FaceMakerBullseye
  LengthFwd = 0
  LengthRev = 0
  Solid = true
  Symmetric = false
FEATURE [Part::Cut] Cut010002001009
  Base = -> Cut010002001008
  Tool = -> Extrusion031
FEATURE [Part::Cut] Cut010002001010
  Base = -> Cut010002001009
  Tool = -> Extrusion030
FEATURE [Part::Cut] Cut010002001011
  Base = -> Cut010002001010
  Tool = -> Extrusion028
FEATURE [Part::Part2DObjectPython] Wire016  # Draft 2D object (typed FeaturePython)
  ChamferSize = 0
  Closed = true
  End = (48.2411,46.0795,4)
  FilletRadius = 0
  Length = 23.0307
  MakeFace = true
  Placement = pos=(46.4005,46.4665,4) rot=(0,0,1;0rad)
  Points = (4) [(0,0,0),(-4.20648,-5.83743,-2.13425e-11),(2.81477,-7.13213,-2.13425e-11),(1.84056,-0.387058,-2.13425e-11)]
  Start = (46.4005,46.4665,4)
  Subdivisions = 0
  Support = -> [Extrusion029]
FEATURE [Part::Extrusion] Extrusion032
  Base = -> Wire016
  Dir = (-1.0589e-12,7.2111e-12,-4)
  DirMode = 0
  FaceMakerClass = Part::FaceMakerBullseye
  LengthFwd = 0
  LengthRev = 0
  Solid = true
  Symmetric = false
FEATURE [Part::Cut] Cut010002001012
  Base = -> Cut010002001011
  Tool = -> Extrusion032
FEATURE [Part::Feature] Cut010002001012001  label="Cut010002001013"
  shape: bbox 153.8 x 114.1 x 15 mm, 63 faces (baked)
FEATURE [Part::Part2DObjectPython] Rectangle006  # Draft 2D object (typed FeaturePython)
  ChamferSize = 0
  Columns = 1
  FilletRadius = 0
  Height = 47
  Length = 72
  MakeFace = true
  Placement = pos=(-13.1006,-13.0628,4) rot=(0,0,1;0rad)
  Rows = 1
  Support = -> [Cut010002001012]
FEATURE [Part::Part2DObjectPython] Ellipse004  # Draft 2D object (typed FeaturePython)
  FirstAngle = 0
  LastAngle = 0
  MajorRadius = 34.47
  MakeFace = true
  MinorRadius = 17
  Placement = pos=(47.9058,11.4238,4) rot=(0,0,1;1.5708rad)
FEATURE [Part::Part2DObjectPython] Line040  # Draft 2D object (typed FeaturePython)
  ChamferSize = 0
  Closed = false
  End = (47.8931,-23.0462,4)
  FilletRadius = 0
  Length = 34.47
  MakeFace = true
  Placement = pos=(47.9058,11.4238,4) rot=(0,0,1;0rad)
  Points = (2) [(0,0,0),(-0.0127607,-34.47,-6.08402e-14)]
  Start = (47.9058,11.4238,4)
  Subdivisions = 0
FEATURE [Part::Part2DObjectPython] Ellipse005  # Draft 2D object (typed FeaturePython)
  FirstAngle = 0
  LastAngle = 0
  MajorRadius = 34.47
  MakeFace = true
  MinorRadius = 17
  Placement = pos=(-2.10694,11.4207,4) rot=(0,0,1;1.5708rad)
FEATURE [Part::Part2DObjectPython] Ellipse006  # Draft 2D object (typed FeaturePython)
  FirstAngle = 0
  LastAngle = 0
  MajorRadius = 34.47
  MakeFace = true
  MinorRadius = 6
  Placement = pos=(-2.10694,11.4207,4) rot=(0,0,1;1.5708rad)
FEATURE [Part::Part2DObjectPython] Ellipse007  # Draft 2D object (typed FeaturePython)
  FirstAngle = 0
  LastAngle = 0
  MajorRadius = 34.47
  MakeFace = true
  MinorRadius = 6
  Placement = pos=(47.9058,11.4238,4) rot=(0,0,1;1.5708rad)
FEATURE [Part::Extrusion] Extrusion033
  Base = -> Ellipse005
  Dir = (-4.52e-13,8e-14,-4)
  DirMode = 0
  FaceMakerClass = Part::FaceMakerBullseye
  LengthFwd = 0
  LengthRev = 0
  Solid = true
  Symmetric = false
FEATURE [Part::Extrusion] Extrusion034
  Base = -> Ellipse004
  Dir = (-4.509e-13,7.91e-14,-4)
  DirMode = 0
  FaceMakerClass = Part::FaceMakerBullseye
  LengthFwd = 0
  LengthRev = 0
  Solid = true
  Symmetric = false
FEATURE [Part::MultiFuse] Fusion001002003002002002
  Shapes = -> [Cut010002001012001,Extrusion033,Extrusion034]
FEATURE [Part::Feature] Fusion001002003002002002001  label="Fusion001002003002002003"
  shape: bbox 153.8 x 114.1 x 15 mm, 65 faces (baked)
FEATURE [Part::Extrusion] Extrusion035
  Base = -> Ellipse006
  Dir = (-4.52e-13,8e-14,-4)
  DirMode = 0
  FaceMakerClass = Part::FaceMakerBullseye
  LengthFwd = 0
  LengthRev = 0
  Solid = true
  Symmetric = false
FEATURE [Part::Extrusion] Extrusion036
  Base = -> Ellipse007
  Dir = (-4.52e-13,8e-14,-4)
  DirMode = 0
  FaceMakerClass = Part::FaceMakerBullseye
  LengthFwd = 0
  LengthRev = 0
  Solid = true
  Symmetric = false
FEATURE [Part::Cut] Cut010002001012002
  Base = -> Fusion001002003002002002001
  Tool = -> Extrusion035
FEATURE [Part::Cut] Cut010002001012003
  Base = -> Cut010002001012002
  Tool = -> Extrusion036
FEATURE [Part::Part2DObjectPython] Rectangle007  # Draft 2D object (typed FeaturePython)
  ChamferSize = 0
  Columns = 1
  FilletRadius = 0
  Height = 68.94
  Length = 50
  MakeFace = true
  Placement = pos=(-2.10694,-23.0493,4) rot=(0,0,1;0rad)
  Rows = 1
FEATURE [Part::Extrusion] Extrusion037
  Base = -> Rectangle007
  Dir = (-4.509e-13,7.91e-14,-4)
  DirMode = 0
  FaceMakerClass = Part::FaceMakerBullseye
  LengthFwd = 0
  LengthRev = 0
  Solid = true
  Symmetric = false
FEATURE [Part::Cut] Cut010002001012004
  Base = -> Cut010002001012003
  Tool = -> Extrusion037
FEATURE [Part::Part2DObjectPython] Wire018  # Draft 2D object (typed FeaturePython)
  ChamferSize = 0
  Closed = true
  End = (47.627,45.9838,5)
  FilletRadius = 0
  Length = 3.65372
  MakeFace = true
  Placement = pos=(47.3654,45.264,4) rot=(0,0,1;0rad)
  Points = (3) [(0,0,0),(1.072,0.552291,1),(0.261549,0.719772,1)]
  Start = (47.3654,45.264,4)
  Subdivisions = 0
FEATURE [Part::Part2DObjectPython] Ellipse008  # Draft 2D object (typed FeaturePython)
  FirstAngle = 0
  LastAngle = 0
  MajorRadius = 34.63
  MakeFace = true
  MinorRadius = 6
  Placement = pos=(47.5391,11.5764,-4.5751e-11) rot=(0,0,1;1.5708rad)
FEATURE [Part::Box] Box  label="Cube"
  AttacherType = Attacher::AttachEngine3D
  Height = 4
  Length = 10
  Placement = pos=(47.6769,45.8907,-2.1563e-11) rot=(0,0,-1;0.082814rad)
  Width = 3
FEATURE [Part::MultiFuse] Fusion001002003002002002002
  Shapes = -> [Box,Cut010002001012004]
FEATURE [Part::Feature] Fusion001002003002002002002001  label="Fusion001002003002002002003"
  shape: bbox 153.8 x 114.1 x 15 mm, 61 faces (baked)
FEATURE [Part::Part2DObjectPython] Line046  # Draft 2D object (typed FeaturePython)
  ChamferSize = 0
  Closed = false
  End = (47.8932,-22.7289,4)
  FilletRadius = 0
  Length = 0.317278
  MakeFace = true
  Placement = pos=(47.8931,-23.0461,4) rot=(0,0,1;0rad)
  Points = (2) [(0,0,0),(0.000119829,0.317278,2.29488e-11)]
  Start = (47.8931,-23.0461,4)
  Subdivisions = 0
FEATURE [Part::Extrusion] Extrusion038
  Base = -> Ellipse008
  Dir = (4.509e-13,-7.91e-14,4)
  DirMode = 0
  FaceMakerClass = Part::FaceMakerBullseye
  LengthFwd = 0
  LengthRev = 0
  Solid = true
  Symmetric = false
FEATURE [Part::Part2DObjectPython] Ellipse009  # Draft 2D object (typed FeaturePython)
  FirstAngle = 0
  LastAngle = 0
  MajorRadius = 26.85
  MakeFace = true
  MinorRadius = 5
  Placement = pos=(22.8994,43.9037,-1.3847e-11) rot=(1,0,0;3.14159rad)
FEATURE [Part::Part2DObjectPython] Line049  # Draft 2D object (typed FeaturePython)
  ChamferSize = 0
  Closed = false
  End = (22.8994,112.147,-1.0169e-12)
  FilletRadius = 0
  Length = 66.5431
  MakeFace = true
  Placement = pos=(22.8994,45.6037,-1.3527e-11) rot=(1,0,0;3.14159rad)
  Points = (2) [(0,0,0),(-3.55271e-15,-66.5431,0)]
  Start = (22.8994,45.6037,-1.3527e-11)
  Subdivisions = 0
FEATURE [Part::Part2DObjectPython] Line050  # Draft 2D object (typed FeaturePython)
  ChamferSize = 0
  Closed = false
  End = (22.8994,49.4037,-1.28126e-11)
  FilletRadius = 0
  Length = 3.8
  MakeFace = true
  Placement = pos=(22.8994,45.6037,-1.3527e-11) rot=(1,0,0;3.14159rad)
  Points = (2) [(0,0,0),(-6.44782e-07,-3.8,2.16945e-19)]
  Start = (22.8994,45.6037,-1.3527e-11)
  Subdivisions = 0
FEATURE [Part::Box] Box001  label="Cube001"
  AttacherType = Attacher::AttachEngine3D
  Height = 4
  Length = 10
  Placement = pos=(-12.1069,45.667,-1.5237e-11) rot=(0,0,1;0rad)
  Width = 10
FEATURE [Part::MultiFuse] Fusion001002003002002002002002
  Shapes = -> [Box001,Fusion001002003002002002002001]
FEATURE [Part::Feature] Fusion001002003002002002002002001  label="Fusion001002003002002002002003"
  shape: bbox 153.8 x 114.1 x 15 mm, 62 faces (baked)
FEATURE [Part::Box] Box002  label="Cube002"
  AttacherType = Attacher::AttachEngine3D
  Height = 4
  Length = 5
  Placement = pos=(-3.62619,45.667,-1.5237e-11) rot=(0,0,1;0rad)
  Width = 5
FEATURE [Part::Box] Box003  label="Cube003"
  AttacherType = Attacher::AttachEngine3D
  Height = 4
  Length = 5
  Placement = pos=(43.2242,45.8452,-2.19238e-11) rot=(0,0,1;0rad)
  Width = 5
FEATURE [Part::MultiFuse] Fusion001002003002002002002002002
  Shapes = -> [Box003,Box002,Fusion001002003002002002002002001]
FEATURE [Part::Feature] Fusion001002003002002002002002002001  label="Fusion001002003002002002002002003"
  shape: bbox 153.8 x 114.1 x 15 mm, 60 faces (baked)
FEATURE [Part::Box] Box004  label="Cube004"
  AttacherType = Attacher::AttachEngine3D
  Height = 4
  Length = 10
  Placement = pos=(-8.62619,44.367,-1.5237e-11) rot=(0,0,1;0rad)
  Width = 1.3
FEATURE [Part::Box] Box005  label="Cube005"
  AttacherType = Attacher::AttachEngine3D
  Height = 4
  Length = 10
  Placement = pos=(43.2242,44.2452,-2.19238e-11) rot=(0,0,1;0rad)
  Width = 1.6
FEATURE [Part::MultiFuse] Fusion001002003002002002002002002002
  Shapes = -> [Box004,Fusion001002003002002002002002002001,Box005]
FEATURE [Part::Feature] Fusion001002003002002002002002002002001  label="Fusion001002003002002002002002002003"
  shape: bbox 153.8 x 114.1 x 15 mm, 60 faces (baked)
FEATURE [Part::Extrusion] Extrusion039
  Base = -> Ellipse009
  Dir = (3.2263e-12,-2.8261e-12,15)
  DirMode = 0
  FaceMakerClass = Part::FaceMakerBullseye
  LengthFwd = 0
  LengthRev = 0
  Solid = true
  Symmetric = false
FEATURE [Part::Cut] Cut010002001012005
  Base = -> Fusion001002003002002002002002002002001
  Tool = -> Extrusion039
FEATURE [Part::Part2DObjectPython] Ellipse010  # Draft 2D object (typed FeaturePython)
  FirstAngle = 0
  LastAngle = 0
  MajorRadius = 40
  MakeFace = true
  MinorRadius = 37.7
  Placement = pos=(56.8337,0.0657738,4.26342) rot=(0,0,1;1.5708rad)
  Support = -> [Cut010002001012005]
FEATURE [Part::Part2DObjectPython] Ellipse011  # Draft 2D object (typed FeaturePython)
  FirstAngle = 0
  LastAngle = 0
  MajorRadius = 40
  MakeFace = true
  MinorRadius = 37.7
  Placement = pos=(-11.2576,0.304714,4.19646) rot=(0,0,1;1.5708rad)
  Support = -> [Cut010002001012005]
FEATURE [Part::Part2DObjectPython] Rectangle008  # Draft 2D object (typed FeaturePython)
  ChamferSize = 0
  Columns = 1
  FilletRadius = 0
  Height = 61.164
  Length = 129.59
  MakeFace = true
  Placement = pos=(-26.4534,82.7702,38.8175) rot=(0.57735,-0.57735,0.57735;4.18879rad)
  Rows = 1
FEATURE [Part::Part2DObjectPython] Rectangle009  # Draft 2D object (typed FeaturePython)
  ChamferSize = 0
  Columns = 1
  FilletRadius = 0
  Height = 61.164
  Length = 129.59
  MakeFace = true
  Placement = pos=(72.8874,83.5507,38.8175) rot=(0.57735,-0.57735,0.57735;4.18879rad)
  Rows = 1
FEATURE [Part::Extrusion] Extrusion040
  Base = -> Ellipse011
  Dir = (3.9468e-12,-9.001e-13,34.621)
  DirMode = 0
  FaceMakerClass = Part::FaceMakerBullseye
  LengthFwd = 0
  LengthRev = 0
  Placement = pos=(-1.975e-12,-9.7441e-09,-17.3105) rot=(0,0,1;0rad)
  Solid = true
  Symmetric = false
FEATURE [Part::Extrusion] Extrusion041
  Base = -> Ellipse010
  Dir = (3.9267e-12,-9.068e-13,34.554)
  DirMode = 0
  FaceMakerClass = Part::FaceMakerBullseye
  LengthFwd = 0
  LengthRev = 0
  Placement = pos=(-1.968e-12,-9.74411e-09,-17.277) rot=(0,0,1;0rad)
  Solid = true
  Symmetric = false
FEATURE [Part::Part2DObjectPython] Rectangle010  # Draft 2D object (typed FeaturePython)
  ChamferSize = 0
  Columns = 1
  FilletRadius = 0
  Height = 129.824
  Length = 215.502
  MakeFace = true
  Placement = pos=(-79.8789,-23.0493,70.5568) rot=(-1,0,0;1.5708rad)
  Rows = 1
  Support = -> [Cut010002001012005]
FEATURE [Part::FeaturePython] Slice  # WARN: FeaturePython — macro-defined, semantics opaque (R4)
  Base = -> Extrusion040
  Mode = 1
  Tolerance = 0
  Tools = -> [Rectangle010]
FEATURE [Part::FeaturePython] Slice_child0  label="Slice.0"  # WARN: FeaturePython — macro-defined, semantics opaque (R4)
  Base = -> Slice
  FilterType = 1
  Invert = false
  OverrideMaxVal = 0
  WindowFrom = 80
  WindowTo = 100
  items = 0
FEATURE [App::DocumentObjectGroup] GrExplode_Slice  label="Exploded Slice"
  Group = -> [Slice_child0]
FEATURE [Part::FeaturePython] Slice001  # WARN: FeaturePython — macro-defined, semantics opaque (R4)
  Base = -> Slice_child0
  Mode = 1
  Tolerance = 0
  Tools = -> [Rectangle008]
FEATURE [Part::FeaturePython] Slice001_child1  label="Slice001.1"  # WARN: FeaturePython — macro-defined, semantics opaque (R4)
  Base = -> Slice001
  FilterType = 1
  Invert = false
  OverrideMaxVal = 0
  WindowFrom = 80
  WindowTo = 100
  items = 1
FEATURE [Part::FeaturePython] Slice002  # WARN: FeaturePython — macro-defined, semantics opaque (R4)
  Base = -> Extrusion041
  Mode = 1
  Tolerance = 0
  Tools = -> [Rectangle009]
FEATURE [Part::FeaturePython] Slice002_child1  label="Slice002.1"  # WARN: FeaturePython — macro-defined, semantics opaque (R4)
  Base = -> Slice002
  FilterType = 1
  Invert = false
  OverrideMaxVal = 0
  WindowFrom = 80
  WindowTo = 100
  items = 1
FEATURE [App::DocumentObjectGroup] GrExplode_Slice002  label="Exploded Slice002"
  Group = -> [Slice002_child1]
FEATURE [Part::Part2DObjectPython] Rectangle011  # Draft 2D object (typed FeaturePython)
  ChamferSize = 0
  Columns = 1
  FilletRadius = 0
  Height = 177.877
  Length = 160.164
  MakeFace = true
  Placement = pos=(-30.0213,-23.0493,93.488) rot=(-1,0,0;1.5708rad)
  Rows = 1
FEATURE [Part::FeaturePython] Slice003  # WARN: FeaturePython — macro-defined, semantics opaque (R4)
  Base = -> Slice002_child1
  Mode = 1
  Tolerance = 0
  Tools = -> [Rectangle011]
FEATURE [App::DocumentObjectGroup] GrExplode_Slice003  label="Exploded Slice003"
FEATURE [Part::FeaturePython] Slice003_child1  label="Slice003.1"  # WARN: FeaturePython — macro-defined, semantics opaque (R4)
  Base = -> Slice003
  FilterType = 1
  Invert = false
  OverrideMaxVal = 0
  WindowFrom = 80
  WindowTo = 100
  items = 1
FEATURE [Part::Cut] Cut010002001012006
  Base = -> Cut010002001012005
  Tool = -> Slice003_child1
FEATURE [Part::Cut] Cut010002001012007
  Base = -> Cut010002001012006
  Tool = -> Slice001_child1
FEATURE [App::DocumentObjectGroup] GrExplode_Slice001  label="Exploded Slice001"
  Group = -> [Cut010002001012007]
FEATURE [Part::Feature] Cut010002001012007001  label="Cut010002001012008"
  shape: bbox 153.8 x 114.1 x 15 mm, 63 faces (baked)
FEATURE [Part::Feature] Cut010002001012007001_solid  label="Cut010002001012008 (Solid)"
  shape: bbox 153.8 x 114.1 x 15 mm, 63 faces (baked)
FEATURE [Part::Feature] Cut010002001012007001_solid001  label="Cut010002001012008 (Solid)001"
  shape: bbox 153.8 x 114.1 x 15 mm, 63 faces (baked)
FEATURE [Part::Part2DObjectPython] Wire019  # Draft 2D object (typed FeaturePython)
  ChamferSize = 0
  Closed = true
  End = (-14.7357,50.1508,15)
  FilletRadius = 0
  Length = 69.9209
  MakeFace = true
  Placement = pos=(-16.5677,56.8454,15) rot=(0,0,1;0rad)
  Points = (8) [(0,0,0),(8.81629,8.81629,2.13518e-12),(12.2786,-3.83595,8.41993e-12),(18.5326,-9.3205,1.27738e-11),(18.6403,-9.71409,8.95817e-12),+3 more]
  Start = (-16.5677,56.8454,15)
  Subdivisions = 0
  Support = -> [Cut010002001012007001_solid001]
FEATURE [Part::Extrusion] Extrusion042
  Base = -> Wire019
  Dir = (3.61e-13,-6.265e-13,-5.5)
  DirMode = 0
  FaceMakerClass = Part::FaceMakerBullseye
  LengthFwd = 0
  LengthRev = 0
  Placement = pos=(2.5788e-12,4.974e-13,-5.5) rot=(0,0,1;0rad)
  Solid = true
  Symmetric = false
FEATURE [Part::MultiFuse] Fusion001002003002002002002002002002002
  Shapes = -> [Cut010002001012007001_solid001,Extrusion042]
